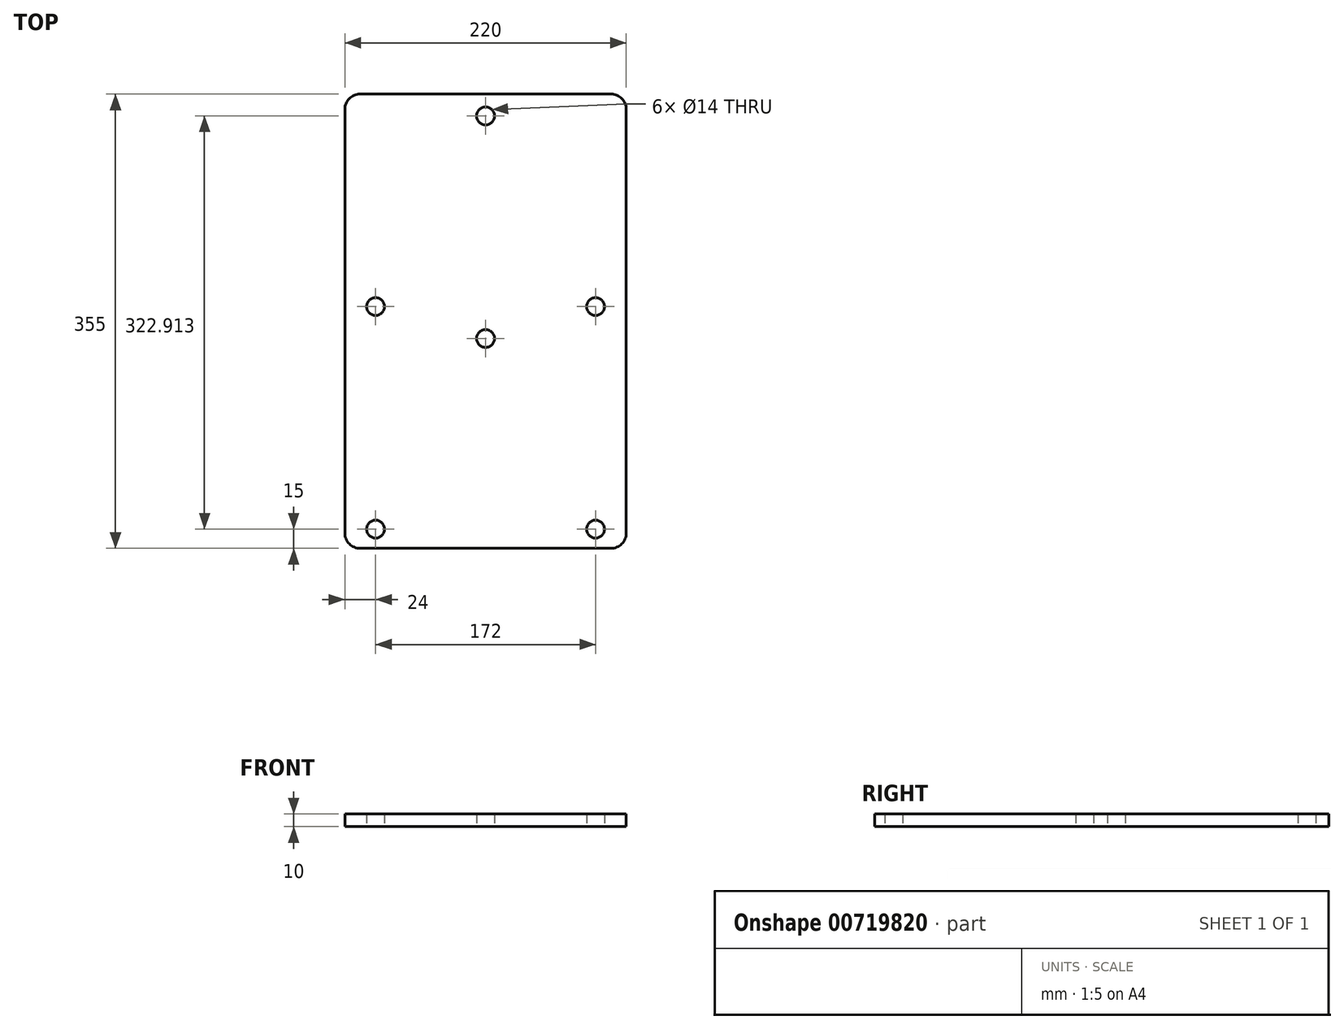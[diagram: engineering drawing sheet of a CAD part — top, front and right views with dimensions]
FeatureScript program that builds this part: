
annotation { "Feature Type Name" : "Feature", "Feature Type Description" : "" }
export const myFeature = defineFeature(function(context is Context, id is Id, definition is map)
    precondition{}
    {
        {
            var Q0;
            Q0=qCreatedBy(makeId("Top.planeOp"),FACE);
            var sketch = newSketch(context, id + "F0", { "sketchPlane" : qUnion([Q0])});
            skLineSegment(sketch, "E0.bottom", {"start": v(12, 0) * mm, "end": v(208, 0) * mm});
            skLineSegment(sketch, "E0.top", {"start": v(12, 355) * mm, "end": v(208, 355) * mm});
            skLineSegment(sketch, "E0.left", {"start": v(0, 12) * mm, "end": v(0, 343) * mm});
            skLineSegment(sketch, "E0.right", {"start": v(220, 12) * mm, "end": v(220, 343) * mm});
            skCircle(sketch, "E1", {"center": v(24, 15) * mm, "radius": 7 * mm});
            skCircle(sketch, "E2", {"center": v(196, 15) * mm, "radius": 7 * mm});
            skCircle(sketch, "E3", {"center": v(110, 163.96) * mm, "radius": 7 * mm});
            skPoint(sketch, "E3.centerSnap0", {"position": v(110, 0) * mm});
            skCircle(sketch, "E4", {"center": v(24, 188.96) * mm, "radius": 7 * mm});
            skCircle(sketch, "E5", {"center": v(196, 188.96) * mm, "radius": 7 * mm});
            skCircle(sketch, "E6", {"center": v(110, 337.91) * mm, "radius": 7 * mm});
            skPoint(sketch, "E7.visualSharp", {"position": v(0, 355) * mm});
            skArc(sketch, "E7.filletArc", {"start": v(12, 355) * mm, "mid": v(3.51, 351.49) * mm, "end": v(0, 343) * mm});
            skPoint(sketch, "E8.visualSharp", {"position": v(220, 355) * mm});
            skArc(sketch, "E8.filletArc", {"start": v(220, 343) * mm, "mid": v(216.49, 351.49) * mm, "end": v(208, 355) * mm});
            skPoint(sketch, "E9.visualSharp", {"position": v(220, 0) * mm});
            skArc(sketch, "E9.filletArc", {"start": v(208, 0) * mm, "mid": v(216.49, 3.51) * mm, "end": v(220, 12) * mm});
            skPoint(sketch, "E10.visualSharp", {"position": v(0, 0) * mm});
            skArc(sketch, "E10.filletArc", {"start": v(0, 12) * mm, "mid": v(3.51, 3.51) * mm, "end": v(12, 0) * mm});
            skSolve(sketch);
        }
        {
            var Q0;
            Q0=makeQuery(id+"F0.imprint","IMPRINT",FACE,{"disambiguationData":[TD([[makeQuery(id+"F0.imprint","IMPRINT",EDGE,{"derivedFrom":sQuery(id+"F0.wireOp",EDGE,"E0.bottom")}),1.0]])]});
            extrude(context, id + "F1", {"entities" : qUnion([Q0]), "depth" : 10 * mm, "offsetDistance" : 25 * mm});
        }
    });
